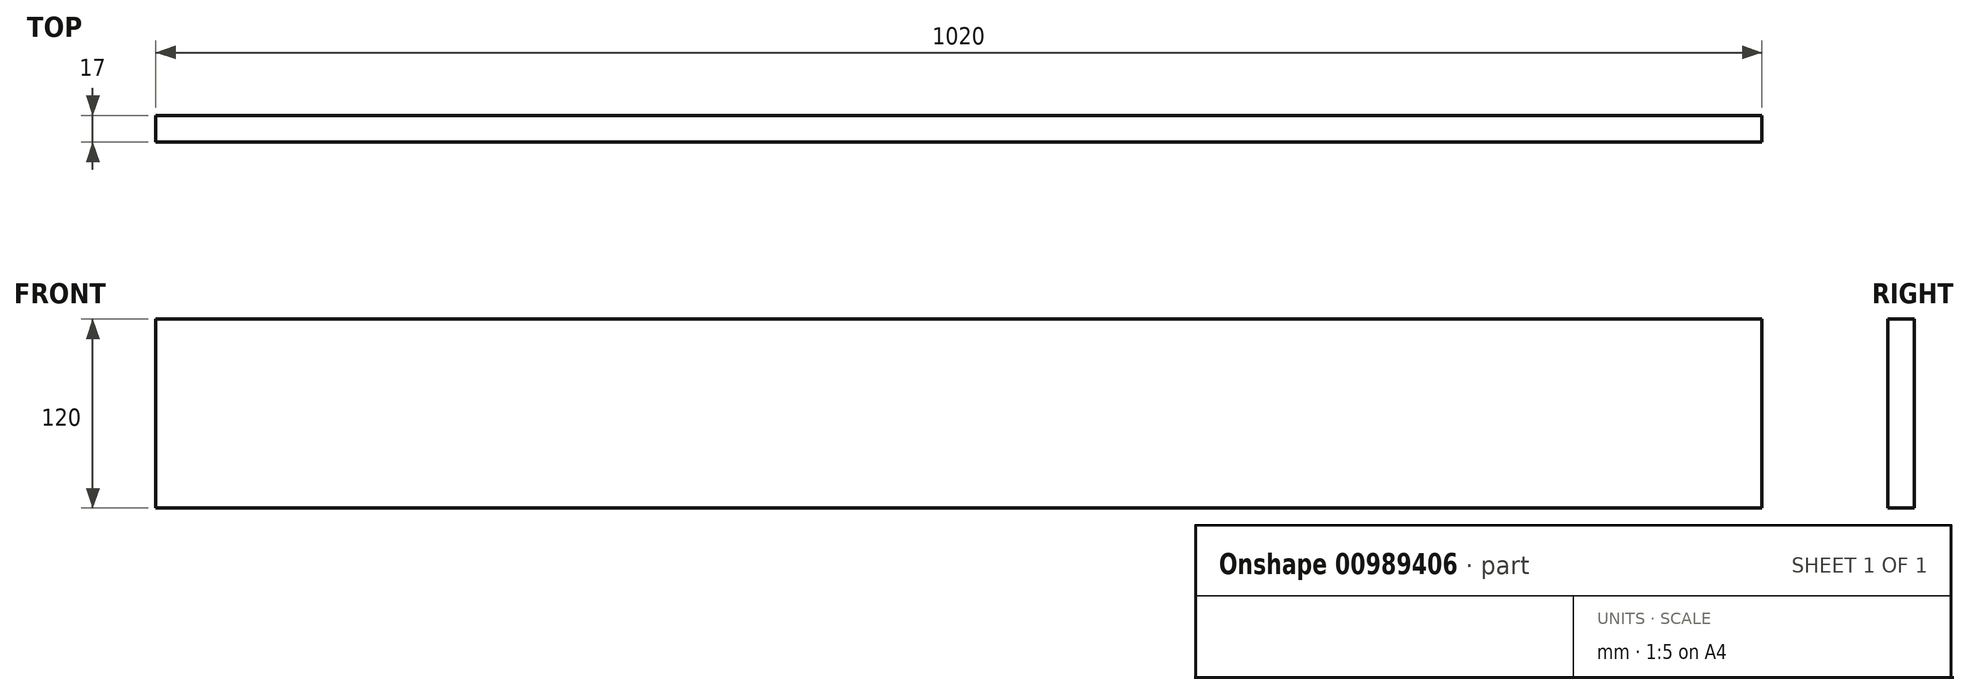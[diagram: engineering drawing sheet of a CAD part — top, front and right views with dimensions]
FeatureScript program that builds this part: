
annotation { "Feature Type Name" : "Feature", "Feature Type Description" : "" }
export const myFeature = defineFeature(function(context is Context, id is Id, definition is map)
    precondition{}
    {
        {
            var Q0;
            Q0=qCreatedBy(makeId("Front.planeOp"),FACE);
            var sketch = newSketch(context, id + "F0", { "sketchPlane" : qUnion([Q0])});
            skLineSegment(sketch, "E0.bottom", {"start": v(416.82, -24.3) * mm, "end": v(-603.18, -24.3) * mm});
            skLineSegment(sketch, "E0.top", {"start": v(416.82, 95.7) * mm, "end": v(-603.18, 95.7) * mm});
            skLineSegment(sketch, "E0.left", {"start": v(416.82, -24.3) * mm, "end": v(416.82, 95.7) * mm});
            skLineSegment(sketch, "E0.right", {"start": v(-603.18, -24.3) * mm, "end": v(-603.18, 95.7) * mm});
            skPoint(sketch, "E0.middle", {"position": v(-93.18, 35.7) * mm});
            skSolve(sketch);
        }
        {
            var Q0;
            Q0 = qSketchRegion(id + "F0", true);
            extrude(context, id + "F1", {"entities" : qUnion([Q0]), "depth" : 17 * mm, "offsetDistance" : 25 * mm});
        }
    });
